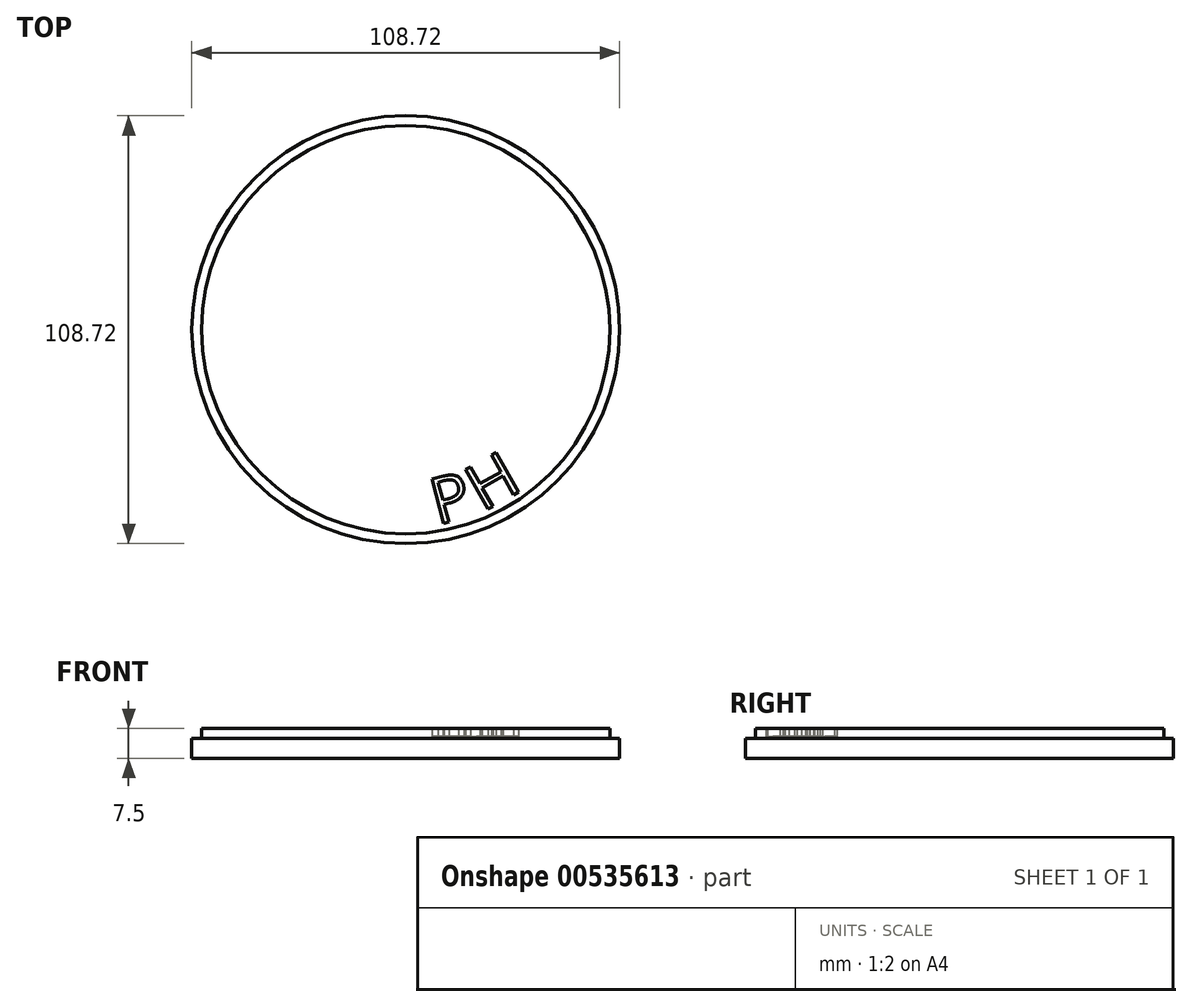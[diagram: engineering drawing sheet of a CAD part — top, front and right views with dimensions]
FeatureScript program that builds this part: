
annotation { "Feature Type Name" : "Feature", "Feature Type Description" : "" }
export const myFeature = defineFeature(function(context is Context, id is Id, definition is map)
    precondition{}
    {
        {
            var Q0;
            Q0=qCreatedBy(makeId("Top.planeOp"),FACE);
            var sketch = newSketch(context, id + "F0", { "sketchPlane" : qUnion([Q0])});
            skCircle(sketch, "E0", {"center": v(0, 0) * mm, "radius": 54.36 * mm});
            skSolve(sketch);
        }
        {
            var Q0;
            Q0 = qSketchRegion(id + "F0", true);
            extrude(context, id + "F1", {"entities" : qUnion([Q0]), "depth" : 5 * mm, "offsetDistance" : 25 * mm});
        }
        {
            var Q0;
            Q0=makeQuery(id+"F1.opExtrude","CAP_FACE",FACE,{"disambiguationData":[OSD([sQuery(id+"F0.wireOp",EDGE,"E0")])],"isStart":false});
            shell(context, id + "F2", {"entities" : qUnion([Q0]), "thickness" : 2.5 * mm});
        }
        {
            var Q0;
            {var subQ0=sQuery(id+"F0.wireOp",EDGE,"E0");Q0=makeQuery(id+"F2.opShell","OFFSET_FACE",FACE,{"disambiguationData":[OSD([subQ0]),TDD([makeQuery(id+"F1.opExtrude","CAP_FACE",FACE,{"disambiguationData":[OSD([subQ0])],"isStart":true})])]});}
            var sketch = newSketch(context, id + "F3", { "sketchPlane" : qUnion([Q0])});
            skText(sketch, "E1", { "text": "P", "fontName": "OpenSans-Regular.ttf"});
            skCircle(sketch, "E2", {"center": v(0, 0) * mm, "radius": 50 * mm, "construction": true});
            skText(sketch, "E3", { "text": "H", "fontName": "OpenSans-Regular.ttf"});
            const initialGuessF3  = {"E1": [0.00811, -0.0496, 0.96593, 0.25882, 0.0117], "E3": [0.01954, -0.04638, 0.87134, 0.49068, 0.0117]};
            skSetInitialGuess(sketch, initialGuessF3);
            skSolve(sketch);
        }
        {
            var Q0;
            Q0=makeQuery(id+"F3.imprint","IMPRINT",FACE,{"disambiguationData":[TD([[makeQuery(id+"F3.imprint","IMPRINT",EDGE,{"derivedFrom":sQuery(id+"F3.wireOp",EDGE,"E3.sketch_text.stroke-0")}),-1.0]])]});
            var Q1;
            Q1=makeQuery(id+"F3.imprint","IMPRINT",FACE,{"disambiguationData":[TD([[makeQuery(id+"F3.imprint","IMPRINT",EDGE,{"derivedFrom":sQuery(id+"F3.wireOp",EDGE,"E1.sketch_text.stroke-0")}),-1.0]])]});
            extrude(context, id + "F4", {"entities" : qUnion([Q0, Q1]), "operationType" : NewBodyOperationType.ADD, "depth" : 3 * mm, "offsetDistance" : 25 * mm});
        }
        {
            var Q0;
            {var subQ0=sQuery(id+"F0.wireOp",EDGE,"E0");Q0=makeQuery(id+"F4.boolean.opBoolean","SPLIT",FACE,{"disambiguationData":[TD([makeQuery(id+"F4.opExtrude","SWEPT_FACE",FACE,{"disambiguationData":[OSD([sQuery(id+"F3.wireOp",EDGE,"E1.sketch_text.stroke-0")])]})])],"derivedFrom":makeQuery(id+"F2.opShell","OFFSET_FACE",FACE,{"disambiguationData":[OSD([subQ0]),TDD([makeQuery(id+"F1.opExtrude","CAP_FACE",FACE,{"disambiguationData":[OSD([subQ0])],"isStart":true})])]})});}
            var Q1;
            {var subQ0=sQuery(id+"F0.wireOp",EDGE,"E0");Q1=makeQuery(id+"F4.boolean.opBoolean","SPLIT",FACE,{"disambiguationData":[TD([makeQuery(id+"F4.opExtrude","SWEPT_FACE",FACE,{"disambiguationData":[OSD([sQuery(id+"F3.wireOp",EDGE,"E1.sketch_text.stroke-8")])]})])],"derivedFrom":makeQuery(id+"F2.opShell","OFFSET_FACE",FACE,{"disambiguationData":[OSD([subQ0]),TDD([makeQuery(id+"F1.opExtrude","CAP_FACE",FACE,{"disambiguationData":[OSD([subQ0])],"isStart":true})])]})});}
            extrude(context, id + "F5", {"entities" : qUnion([Q0, Q1]), "operationType" : NewBodyOperationType.ADD, "depth" : 5 * mm, "offsetDistance" : 25 * mm});
        }
    });
